# Revit family: Shower-Door-KOHLER-Composed-K-706081
name_source: partatom
category: Specialty Equipment
revit_build: Autodesk Revit 2017 (Build: 20160225_1515(x64)
units: mm (PartAtom-declared; Revit-internal decimal feet)

## family parameters
Cut with Voids When Loaded = No
Host = Face
OmniClass Number = 23.31.17.17
OmniClass Title = Shower Enclosures
Part Type = Normal
Room Calculation Point = No
Round Connector Dimension = Use Diameter
Shared = No

## types (1)
- SHP-Bright Polished Silver
    ADA Compliant = No
    Assembly Code = C1030200
    Date Modified = 08/13/2021
    Default Elevation = 0"
    Description = Sliding shower door, 78 Inch H x 56-1/8 - 59-7/8Inch W, with 3/8 Inch thick Crystal Clear glass
    Finish = Kohler-Metal-SHP-Bright_Polished_Silver
    Height = 78"
    Length = 4 1/4"
    Manufacturer = KOHLER Co.
    Master Format 2014 = 10 28 19.16
    Master Format 2014 Name = Shower Doors
    Material = Premium Metal Construction
    Model = K-706081-L-SHP
    Product Documentation Link = https://www.us.kohler.com
    Product Name = Composed
    Product Page URL = https://www.us.kohler.com
    Type = 1
    URL = https://www.us.kohler.com
    WaterSense Certified = No

## geometry (parser evidence)
native form markers: Sweep x4
no freeform markers — native parametric forms only
